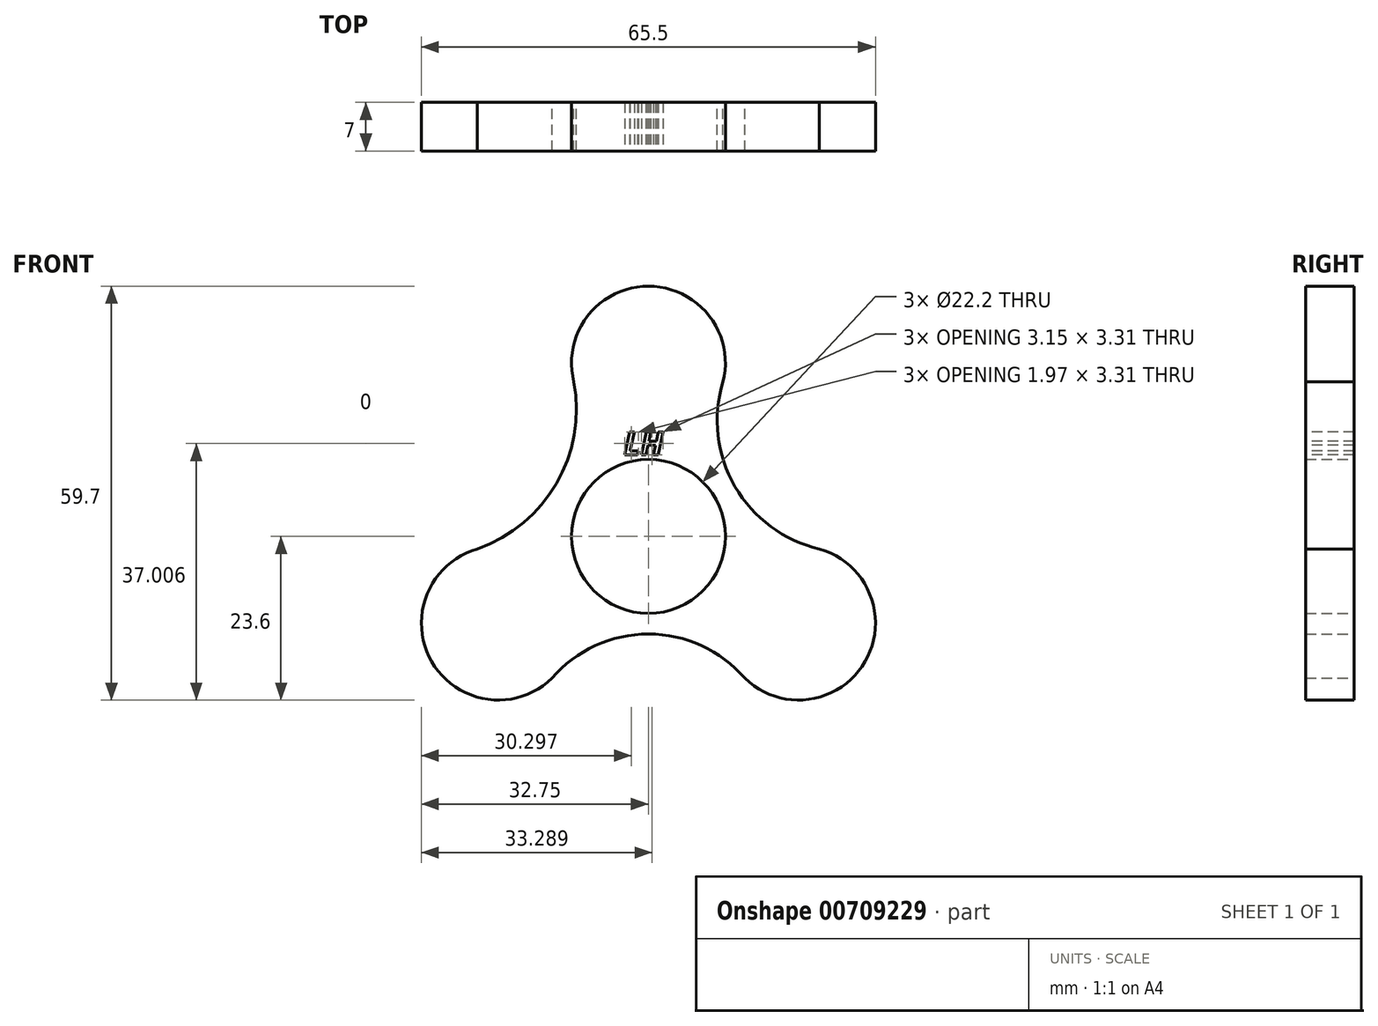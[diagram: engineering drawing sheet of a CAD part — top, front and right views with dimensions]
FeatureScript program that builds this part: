
annotation { "Feature Type Name" : "Feature", "Feature Type Description" : "" }
export const myFeature = defineFeature(function(context is Context, id is Id, definition is map)
    precondition{}
    {
        {
            var Q0;
            Q0=qCreatedBy(makeId("Front.planeOp"),FACE);
            var sketch = newSketch(context, id + "F0", { "sketchPlane" : qUnion([Q0])});
            skCircle(sketch, "E0", {"center": v(0, 0) * mm, "radius": 11.1 * mm});
            skCircle(sketch, "E1", {"center": v(0, 25) * mm, "radius": 11.1 * mm});
            skCircle(sketch, "E2.1.0", {"center": v(-21.65, -12.5) * mm, "radius": 11.1 * mm});
            skCircle(sketch, "E2.2.0", {"center": v(21.65, -12.5) * mm, "radius": 11.1 * mm});
            skArc(sketch, "E3", {"start": v(-24.67, -1.82) * mm, "mid": v(-13.26, 7.66) * mm, "end": v(-10.76, 22.27) * mm});
            skArc(sketch, "E4", {"start": v(13.91, -20.46) * mm, "mid": v(0, -14.08) * mm, "end": v(-13.91, -20.46) * mm});
            skArc(sketch, "E5", {"start": v(10.76, 22.27) * mm, "mid": v(12.48, 7.2) * mm, "end": v(24.67, -1.82) * mm});
            skSolve(sketch);
        }
        {
            var Q0;
            Q0=makeQuery(id+"F0.imprint","IMPRINT",FACE,{"disambiguationData":[TD([[makeQuery(id+"F0.imprint","IMPRINT",EDGE,{"derivedFrom":sQuery(id+"F0.wireOp",EDGE,"E0")}),-1.0]])]});
            var Q1;
            {var subQ0=sQuery(id+"F0.wireOp",EDGE,"E2.1.0");var subQ1=makeQuery(id+"F0.imprint","INTERSECT",VERTEX,{"derivedFrom":[subQ0,sQuery(id+"F0.wireOp",EDGE,"E3")]});Q1=makeQuery(id+"F0.imprint","IMPRINT",FACE,{"disambiguationData":[TD([[makeQuery(id+"F0.imprint","IMPRINT",EDGE,{"disambiguationData":[TD([[subQ1,1.0]])],"derivedFrom":subQ0}),1.0]])]});}
            var Q2;
            {var subQ0=sQuery(id+"F0.wireOp",EDGE,"E5");var subQ1=sQuery(id+"F0.wireOp",EDGE,"E2.2.0");var subQ2=makeQuery(id+"F0.imprint","INTERSECT",VERTEX,{"disambiguationData":[OD(1.0)],"derivedFrom":[subQ1,subQ0]});Q2=makeQuery(id+"F0.imprint","IMPRINT",FACE,{"disambiguationData":[TD([[makeQuery(id+"F0.imprint","IMPRINT",EDGE,{"disambiguationData":[TD([[subQ2,-1.0]])],"derivedFrom":subQ1}),1.0]])]});}
            var Q3;
            {var subQ0=sQuery(id+"F0.wireOp",EDGE,"E1");var subQ1=makeQuery(id+"F0.imprint","INTERSECT",VERTEX,{"derivedFrom":[subQ0,sQuery(id+"F0.wireOp",EDGE,"E3")]});Q3=makeQuery(id+"F0.imprint","IMPRINT",FACE,{"disambiguationData":[TD([[makeQuery(id+"F0.imprint","IMPRINT",EDGE,{"disambiguationData":[TD([[subQ1,-1.0]])],"derivedFrom":subQ0}),1.0]])]});}
            extrude(context, id + "F1", {"entities" : qUnion([Q0, Q1, Q2, Q3]), "depth" : 7 * mm, "offsetDistance" : 25 * mm});
        }
        {
            var Q0;
            Q0=makeQuery(id+"F1.opExtrude","CAP_FACE",FACE,{"disambiguationData":[OSD([sQuery(id+"F0.wireOp",EDGE,"E0"),sQuery(id+"F0.wireOp",EDGE,"E1"),sQuery(id+"F0.wireOp",EDGE,"E2.1.0"),sQuery(id+"F0.wireOp",EDGE,"E2.2.0"),sQuery(id+"F0.wireOp",EDGE,"E3"),sQuery(id+"F0.wireOp",EDGE,"E4"),sQuery(id+"F0.wireOp",EDGE,"E5")])],"isStart":false});
            var sketch = newSketch(context, id + "F2", { "sketchPlane" : qUnion([Q0])});
            skText(sketch, "E6", { "text": "LH", "fontName": "OpenSans-BoldItalic.ttf"});
            const initialGuessF2  = {"E6": [-0.00356, 0.01175, 1, 0, 0.00334]};
            skSetInitialGuess(sketch, initialGuessF2);
            skSolve(sketch);
        }
        {
            var Q0;
            Q0 = qSketchRegion(id + "F2", true);
            extrude(context, id + "F3", {"entities" : qUnion([Q0]), "operationType" : NewBodyOperationType.REMOVE, "oppositeDirection" : true, "depth" : 12.7 * mm, "offsetDistance" : 25 * mm});
        }
    });
